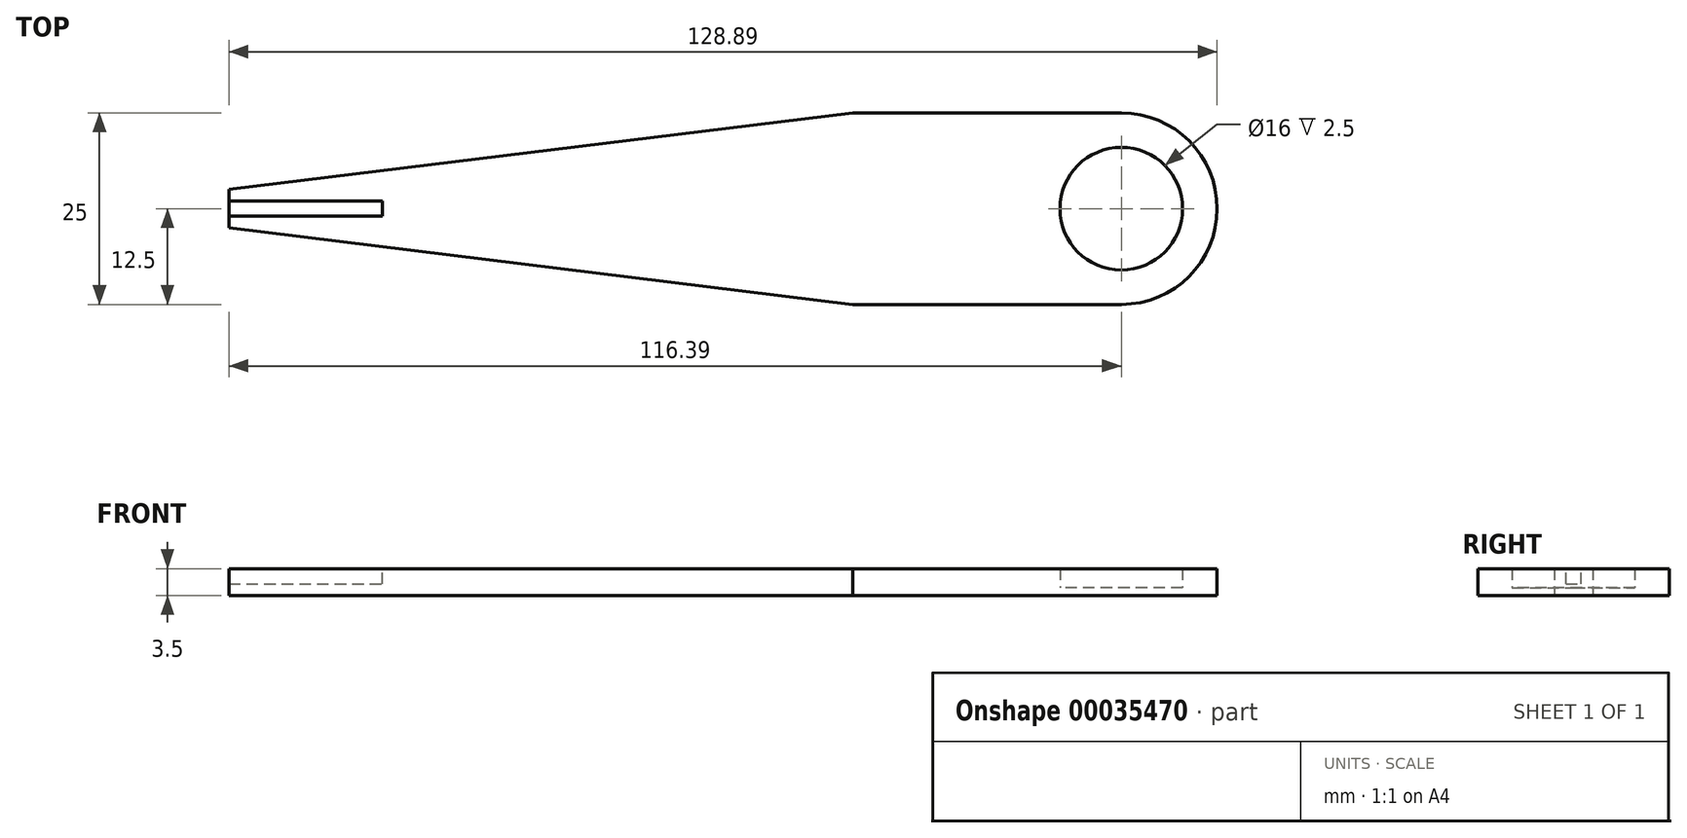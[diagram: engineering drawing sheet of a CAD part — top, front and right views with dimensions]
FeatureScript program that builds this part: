
annotation { "Feature Type Name" : "Feature", "Feature Type Description" : "" }
export const myFeature = defineFeature(function(context is Context, id is Id, definition is map)
    precondition{}
    {
        {
            var Q0;
            Q0=qCreatedBy(makeId("Top.planeOp"),FACE);
            var sketch = newSketch(context, id + "F0", { "sketchPlane" : qUnion([Q0])});
            skCircle(sketch, "E0", {"center": v(0, 0) * mm, "radius": 8 * mm});
            skCircle(sketch, "E1", {"center": v(0, 0) * mm, "radius": 12.5 * mm});
            skLineSegment(sketch, "E2", {"start": v(-35, 12.5) * mm, "end": v(0, 12.5) * mm});
            skLineSegment(sketch, "E3", {"start": v(-35, -12.5) * mm, "end": v(0, -12.5) * mm});
            skLineSegment(sketch, "E4", {"start": v(-35, 12.5) * mm, "end": v(-80.23, 12.5) * mm, "construction": true});
            skLineSegment(sketch, "E5", {"start": v(-35, 12.5) * mm, "end": v(-116.39, 2.5) * mm});
            skLineSegment(sketch, "E6", {"start": v(-35, -12.5) * mm, "end": v(-78.86, -12.5) * mm, "construction": true});
            skLineSegment(sketch, "E7", {"start": v(-35, -12.5) * mm, "end": v(-116.39, -2.5) * mm});
            skLineSegment(sketch, "E8", {"start": v(-116.39, -2.5) * mm, "end": v(-116.39, 2.5) * mm});
            skSolve(sketch);
        }
        {
            var Q0;
            Q0 = qSketchRegion(id + "F0", true);
            extrude(context, id + "F1", {"entities" : qUnion([Q0]), "depth" : 3.5 * mm});
        }
        {
            var Q0;
            Q0=makeQuery(id+"F0.imprint","IMPRINT",FACE,{"disambiguationData":[TD([[makeQuery(id+"F0.imprint","IMPRINT",EDGE,{"derivedFrom":sQuery(id+"F0.wireOp",EDGE,"E0")}),1.0]])]});
            extrude(context, id + "F2", {"entities" : qUnion([Q0]), "operationType" : NewBodyOperationType.ADD, "depth" : 1 * mm});
        }
        {
            var Q0;
            Q0=makeQuery(id+"F1.opExtrude","CAP_FACE",FACE,{"disambiguationData":[OSD([sQuery(id+"F0.wireOp",EDGE,"E0"),sQuery(id+"F0.wireOp",EDGE,"E1"),sQuery(id+"F0.wireOp",EDGE,"E2"),sQuery(id+"F0.wireOp",EDGE,"E3"),sQuery(id+"F0.wireOp",EDGE,"E5"),sQuery(id+"F0.wireOp",EDGE,"E7"),sQuery(id+"F0.wireOp",EDGE,"E8")])],"isStart":false});
            var sketch = newSketch(context, id + "F3", { "sketchPlane" : qUnion([Q0])});
            skLineSegment(sketch, "E9.bottom", {"start": v(-116.39, 1) * mm, "end": v(-96.39, 1) * mm});
            skLineSegment(sketch, "E9.top", {"start": v(-116.39, -1) * mm, "end": v(-96.39, -1) * mm});
            skLineSegment(sketch, "E9.left", {"start": v(-116.39, 1) * mm, "end": v(-116.39, -1) * mm});
            skLineSegment(sketch, "E9.right", {"start": v(-96.39, 1) * mm, "end": v(-96.39, -1) * mm});
            skSolve(sketch);
        }
        {
            var Q0;
            Q0 = qSketchRegion(id + "F3", true);
            extrude(context, id + "F4", {"entities" : qUnion([Q0]), "operationType" : NewBodyOperationType.REMOVE, "oppositeDirection" : true, "depth" : 2 * mm});
        }
    });
